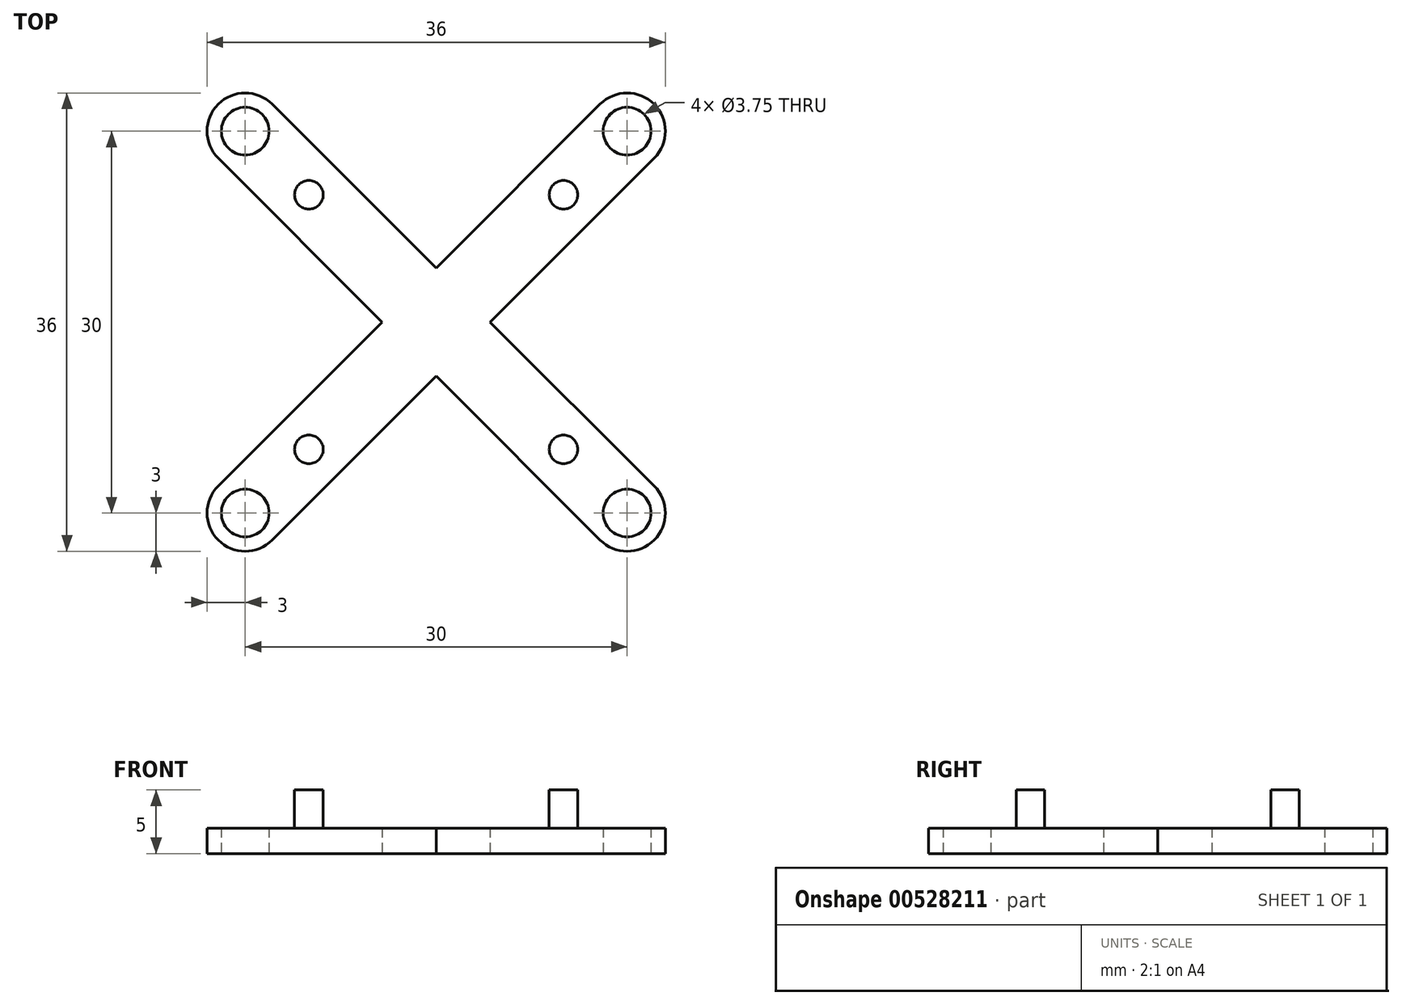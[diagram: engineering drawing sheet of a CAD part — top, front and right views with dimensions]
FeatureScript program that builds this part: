
annotation { "Feature Type Name" : "Feature", "Feature Type Description" : "" }
export const myFeature = defineFeature(function(context is Context, id is Id, definition is map)
    precondition{}
    {
        {
            var Q0;
            Q0=qCreatedBy(makeId("Top.planeOp"),FACE);
            var sketch = newSketch(context, id + "F0", { "sketchPlane" : qUnion([Q0])});
            skLineSegment(sketch, "E0.bottom", {"start": v(0, 0) * mm, "end": v(-36, 0) * mm});
            skLineSegment(sketch, "E0.top", {"start": v(0, 36) * mm, "end": v(-36, 36) * mm});
            skLineSegment(sketch, "E0.left", {"start": v(0, 0) * mm, "end": v(0, 36) * mm});
            skLineSegment(sketch, "E0.right", {"start": v(-36, 0) * mm, "end": v(-36, 36) * mm});
            skCircle(sketch, "E1", {"center": v(-3, 33) * mm, "radius": 1.5 * mm});
            skCircle(sketch, "E2", {"center": v(-3, 3) * mm, "radius": 1.5 * mm});
            skCircle(sketch, "E3", {"center": v(-33, 33) * mm, "radius": 1.5 * mm});
            skCircle(sketch, "E4", {"center": v(-33, 3) * mm, "radius": 1.5 * mm});
            skSolve(sketch);
        }
        {
            var Q0;
            Q0=qCreatedBy(makeId("Top.planeOp"),FACE);
            var sketch = newSketch(context, id + "F1", { "sketchPlane" : qUnion([Q0])});
            skLineSegment(sketch, "E5.bottom", {"start": v(-31.5, 31.5) * mm, "end": v(-4.5, 31.5) * mm});
            skLineSegment(sketch, "E5.top", {"start": v(-31.5, 4.5) * mm, "end": v(-4.5, 4.5) * mm});
            skLineSegment(sketch, "E5.left", {"start": v(-31.5, 31.5) * mm, "end": v(-31.5, 4.5) * mm});
            skLineSegment(sketch, "E5.right", {"start": v(-4.5, 31.5) * mm, "end": v(-4.5, 4.5) * mm});
            skCircle(sketch, "E6", {"center": v(-28, 28) * mm, "radius": 1.5 * mm});
            skCircle(sketch, "E7", {"center": v(-8, 28) * mm, "radius": 1.5 * mm});
            skCircle(sketch, "E8", {"center": v(-8, 8) * mm, "radius": 1.5 * mm});
            skCircle(sketch, "E9", {"center": v(-28, 8) * mm, "radius": 1.5 * mm});
            skSolve(sketch);
        }
        {
            var Q0;
            Q0=qCreatedBy(makeId("Top.planeOp"),FACE);
            var sketch = newSketch(context, id + "F2", { "sketchPlane" : qUnion([Q0])});
            skArc(sketch, "E10", {"start": v(-30.88, 35.12) * mm, "mid": v(-35.12, 35.12) * mm, "end": v(-35.12, 30.88) * mm});
            skArc(sketch, "E11", {"start": v(-0.88, 30.88) * mm, "mid": v(-0.88, 35.12) * mm, "end": v(-5.12, 35.12) * mm});
            skArc(sketch, "E12", {"start": v(-5.12, 0.88) * mm, "mid": v(-0.88, 0.88) * mm, "end": v(-0.88, 5.12) * mm});
            skArc(sketch, "E13", {"start": v(-35.12, 5.12) * mm, "mid": v(-35.12, 0.88) * mm, "end": v(-30.88, 0.88) * mm});
            skLineSegment(sketch, "E14", {"start": v(-35.12, 30.88) * mm, "end": v(-22.24, 18) * mm});
            skLineSegment(sketch, "E15", {"start": v(-30.88, 35.12) * mm, "end": v(-18, 22.24) * mm});
            skLineSegment(sketch, "E16", {"start": v(-0.88, 30.88) * mm, "end": v(-13.76, 18) * mm});
            skLineSegment(sketch, "E17", {"start": v(-35.12, 5.12) * mm, "end": v(-22.24, 18) * mm});
            skLineSegment(sketch, "E18.trimOffspring", {"start": v(-18, 13.76) * mm, "end": v(-5.12, 0.88) * mm});
            skLineSegment(sketch, "E19.trimOffspring", {"start": v(-18, 22.24) * mm, "end": v(-5.12, 35.12) * mm});
            skLineSegment(sketch, "E20.trimOffspring", {"start": v(-13.76, 18) * mm, "end": v(-0.88, 5.12) * mm});
            skLineSegment(sketch, "E21.trimOffspring", {"start": v(-18, 13.76) * mm, "end": v(-31.76, 0) * mm});
            skSolve(sketch);
        }
        {
            var Q0;
            Q0=qCreatedBy(makeId("Top.planeOp"),FACE);
            var sketch = newSketch(context, id + "F3", { "sketchPlane" : qUnion([Q0])});
            skCircle(sketch, "E22", {"center": v(-33, 33) * mm, "radius": 1.88 * mm});
            skCircle(sketch, "E23", {"center": v(-3, 33) * mm, "radius": 1.88 * mm});
            skCircle(sketch, "E24", {"center": v(-3, 3) * mm, "radius": 1.88 * mm});
            skCircle(sketch, "E25", {"center": v(-33, 3) * mm, "radius": 1.88 * mm});
            skSolve(sketch);
        }
        {
            var Q0;
            Q0=qCreatedBy(makeId("Top.planeOp"),FACE);
            var sketch = newSketch(context, id + "F4", { "sketchPlane" : qUnion([Q0])});
            skCircle(sketch, "E26", {"center": v(-28, 8) * mm, "radius": 1.13 * mm});
            skCircle(sketch, "E27", {"center": v(-8, 8) * mm, "radius": 1.13 * mm});
            skCircle(sketch, "E28", {"center": v(-8, 28) * mm, "radius": 1.13 * mm});
            skCircle(sketch, "E29", {"center": v(-28, 28) * mm, "radius": 1.13 * mm});
            skSolve(sketch);
        }
        {
            var Q0;
            Q0 = qSketchRegion(id + "F2", true);
            extrude(context, id + "F5", {"entities" : qUnion([Q0]), "depth" : 2 * mm, "offsetDistance" : 25 * mm});
        }
        {
            var Q0;
            Q0 = qSketchRegion(id + "F3", true);
            extrude(context, id + "F6", {"entities" : qUnion([Q0]), "operationType" : NewBodyOperationType.REMOVE, "depth" : 10 * mm, "offsetDistance" : 25 * mm});
        }
        {
            var Q0;
            Q0 = qSketchRegion(id + "F4", true);
            extrude(context, id + "F7", {"entities" : qUnion([Q0]), "operationType" : NewBodyOperationType.ADD, "depth" : 5 * mm, "offsetDistance" : 25 * mm});
        }
    });
